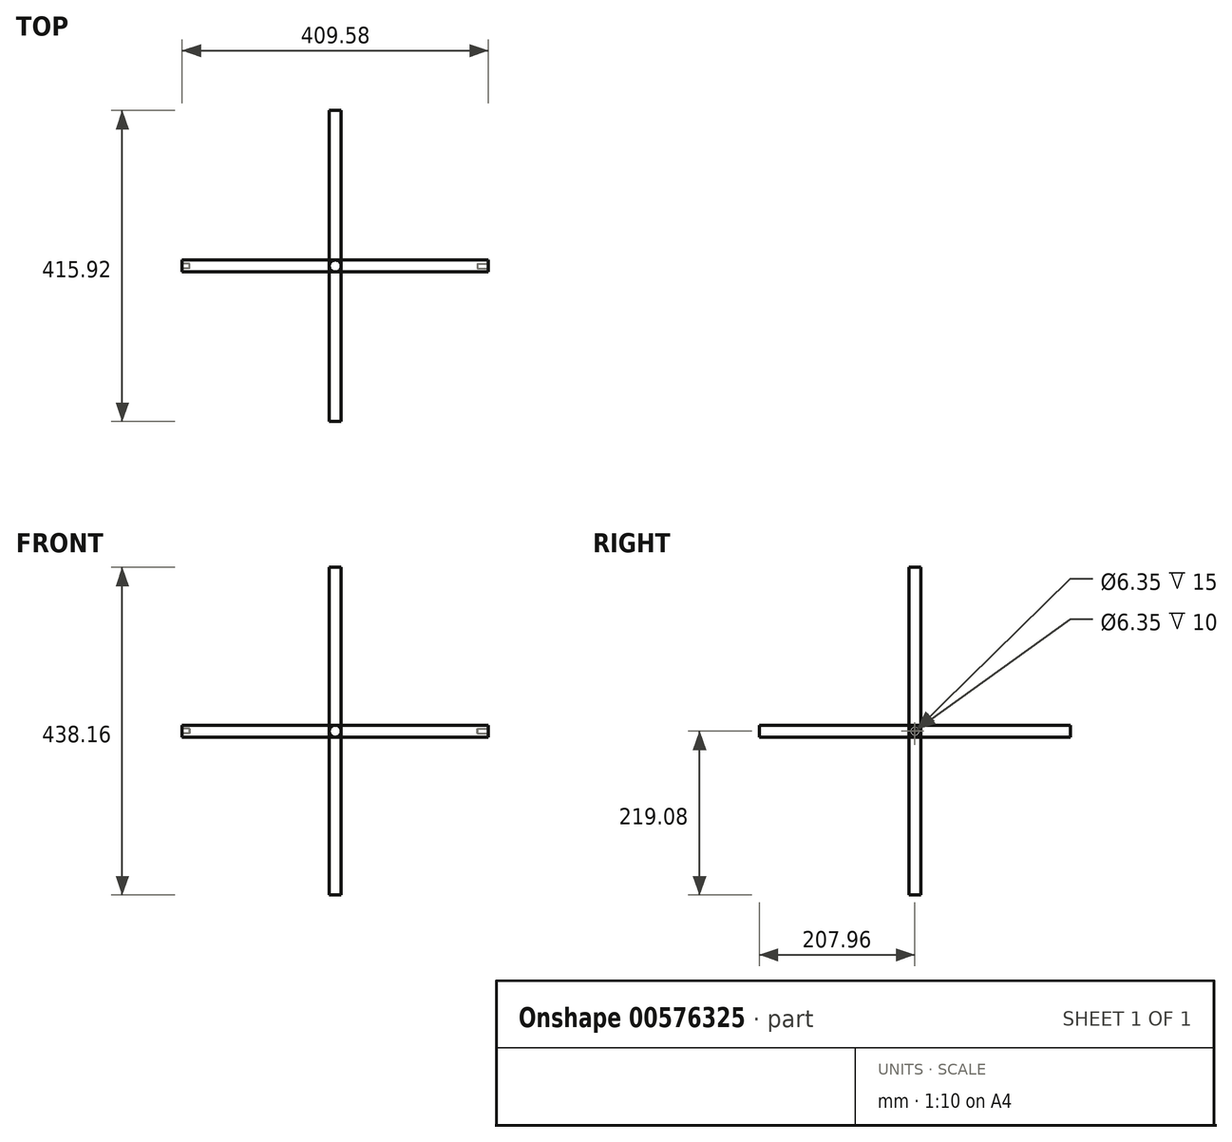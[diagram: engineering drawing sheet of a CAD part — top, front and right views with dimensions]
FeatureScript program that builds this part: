
annotation { "Feature Type Name" : "Feature", "Feature Type Description" : "" }
export const myFeature = defineFeature(function(context is Context, id is Id, definition is map)
    precondition{}
    {
        {
            assignVariable(context, id + "F0", {"name" : "X", "anyValue" : 409.57 * mm});
        }
        {
            assignVariable(context, id + "F1", {"name" : "Y", "anyValue" : 415.92 * mm});
        }
        {
            assignVariable(context, id + "F2", {"name" : "Z", "anyValue" : 438.15 * mm});
        }
        {
            var Q0;
            Q0=qCreatedBy(makeId("Front.planeOp"),FACE);
            var sketch = newSketch(context, id + "F3", { "sketchPlane" : qUnion([Q0]), "asVersion" : FeatureScriptVersionNumber.V686_LOFT_FS_BUG_FIXES});
            skCircle(sketch, "E0", {"center": v(0, 0) * mm, "radius": 7.94 * mm});
            skLineSegment(sketch, "E1", {"start": v(0, 30.75) * mm, "end": v(0, -36) * mm, "construction": true});
            skLineSegment(sketch, "E2", {"start": v(-29.76, 0) * mm, "end": v(29.19, 0) * mm, "construction": true});
            skSolve(sketch);
        }
        {
            var Q0;
            Q0=qSketchRegion(id+"F3",true);
            extrude(context, id + "F4", {"entities" : qUnion([Q0]), "depth" : getVariable(context, 'X'), "offsetDistance" : 25 * mm, "symmetric" : true});
        }
        {
            var Q0;
            Q0=makeQuery(id+"F4.opExtrude","SWEPT_BODY",BODY,{"disambiguationData":[OSD([sQuery(id+"F3.wireOp",EDGE,"E0")])]});
            var Q1;
            Q1=sQuery(id+"F3.wireOp",EDGE,"E1");
            transform(context, id + "F5", {"entities" : qUnion([Q0]), "transformType" : TransformType.ROTATION, "transformAxis" : qUnion([Q1]), "angle" : 90 * degree, "makeCopy" : false});
        }
        {
            var Q0;
            Q0=qSketchRegion(id+"F3",true);
            extrude(context, id + "F6", {"entities" : qUnion([Q0]), "depth" : getVariable(context, 'Y'), "offsetDistance" : 25 * mm, "symmetric" : true});
        }
        {
            var Q0;
            Q0=makeQuery(id+"F4.opExtrude","CAP_FACE",FACE,{"disambiguationData":[OSD([sQuery(id+"F3.wireOp",EDGE,"E0")])],"isStart":true});
            var sketch = newSketch(context, id + "F7", { "sketchPlane" : qUnion([Q0]), "asVersion" : FeatureScriptVersionNumber.V686_LOFT_FS_BUG_FIXES});
            skCircle(sketch, "E3", {"center": v(0, 0) * mm, "radius": 3.18 * mm});
            skSolve(sketch);
        }
        {
            var Q0;
            Q0=qSketchRegion(id+"F7",true);
            extrude(context, id + "F8", {"entities" : qUnion([Q0]), "operationType" : NewBodyOperationType.REMOVE, "oppositeDirection" : true, "depth" : 15 * mm, "offsetDistance" : 25 * mm});
        }
        {
            var Q0;
            Q0=makeQuery(id+"F4.opExtrude","CAP_FACE",FACE,{"disambiguationData":[OSD([sQuery(id+"F3.wireOp",EDGE,"E0")])],"isStart":false});
            var sketch = newSketch(context, id + "F9", { "sketchPlane" : qUnion([Q0]), "asVersion" : FeatureScriptVersionNumber.V686_LOFT_FS_BUG_FIXES});
            skCircle(sketch, "E4", {"center": v(0, 0) * mm, "radius": 3.18 * mm});
            skSolve(sketch);
        }
        {
            var Q0;
            Q0=qSketchRegion(id+"F9",true);
            extrude(context, id + "F10", {"entities" : qUnion([Q0]), "operationType" : NewBodyOperationType.REMOVE, "oppositeDirection" : true, "depth" : 10 * mm, "offsetDistance" : 25 * mm});
        }
        {
            var Q0;
            Q0 = qSketchRegion(id + "F3", true);
            extrude(context, id + "F11", {"entities" : qUnion([Q0]), "depth" : getVariable(context, 'Z'), "offsetDistance" : 25 * mm, "symmetric" : true});
        }
        {
            var Q0;
            Q0=makeQuery(id+"F11.opExtrude","SWEPT_BODY",BODY,{"disambiguationData":[OSD([sQuery(id+"F3.wireOp",EDGE,"E0")])]});
            var Q1;
            Q1=sQuery(id+"F3.wireOp",EDGE,"E2");
            transform(context, id + "F12", {"entities" : qUnion([Q0]), "transformType" : TransformType.ROTATION, "transformAxis" : qUnion([Q1]), "angle" : 90 * degree, "makeCopy" : false});
        }
    });
